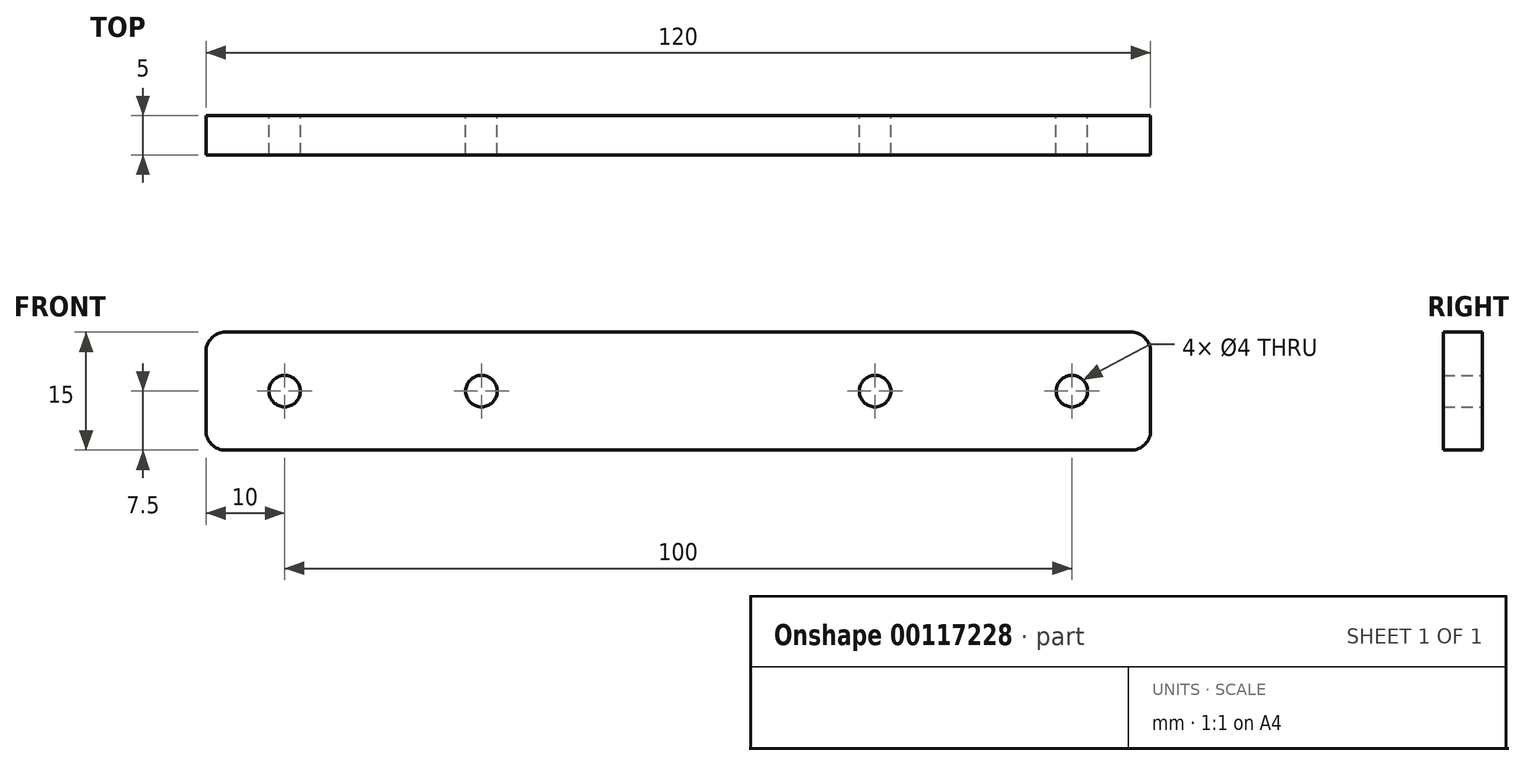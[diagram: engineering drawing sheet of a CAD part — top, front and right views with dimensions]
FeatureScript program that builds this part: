
annotation { "Feature Type Name" : "Feature", "Feature Type Description" : "" }
export const myFeature = defineFeature(function(context is Context, id is Id, definition is map)
    precondition{}
    {
        {
            var Q0;
            Q0=qCreatedBy(makeId("Front.planeOp"),FACE);
            var sketch = newSketch(context, id + "F0", { "sketchPlane" : qUnion([Q0])});
            skLineSegment(sketch, "E0.bottom", {"start": v(57.5, -7.5) * mm, "end": v(-57.5, -7.5) * mm});
            skLineSegment(sketch, "E0.top", {"start": v(57.5, 7.5) * mm, "end": v(-57.5, 7.5) * mm});
            skLineSegment(sketch, "E0.left", {"start": v(60, -5) * mm, "end": v(60, 5) * mm});
            skLineSegment(sketch, "E0.right", {"start": v(-60, -5) * mm, "end": v(-60, 5) * mm});
            skPoint(sketch, "E0.middle", {"position": v(0, 0) * mm});
            skCircle(sketch, "E1", {"center": v(-50, 0) * mm, "radius": 2 * mm});
            skCircle(sketch, "E2", {"center": v(50, 0) * mm, "radius": 2 * mm});
            skCircle(sketch, "E3", {"center": v(-25, 0) * mm, "radius": 2 * mm});
            skCircle(sketch, "E4", {"center": v(25, 0) * mm, "radius": 2 * mm});
            skPoint(sketch, "E5.visualSharp", {"position": v(60, 7.5) * mm});
            skArc(sketch, "E5.filletArc", {"start": v(60, 5) * mm, "mid": v(59.27, 6.77) * mm, "end": v(57.5, 7.5) * mm});
            skPoint(sketch, "E6.visualSharp", {"position": v(60, -7.5) * mm});
            skArc(sketch, "E6.filletArc", {"start": v(57.5, -7.5) * mm, "mid": v(59.27, -6.77) * mm, "end": v(60, -5) * mm});
            skPoint(sketch, "E7.visualSharp", {"position": v(-60, -7.5) * mm});
            skArc(sketch, "E7.filletArc", {"start": v(-60, -5) * mm, "mid": v(-59.27, -6.77) * mm, "end": v(-57.5, -7.5) * mm});
            skPoint(sketch, "E8.visualSharp", {"position": v(-60, 7.5) * mm});
            skArc(sketch, "E8.filletArc", {"start": v(-57.5, 7.5) * mm, "mid": v(-59.27, 6.77) * mm, "end": v(-60, 5) * mm});
            skSolve(sketch);
        }
        {
            var Q0;
            Q0 = qSketchRegion(id + "F0", true);
            extrude(context, id + "F1", {"entities" : qUnion([Q0]), "depth" : 5 * mm});
        }
    });
